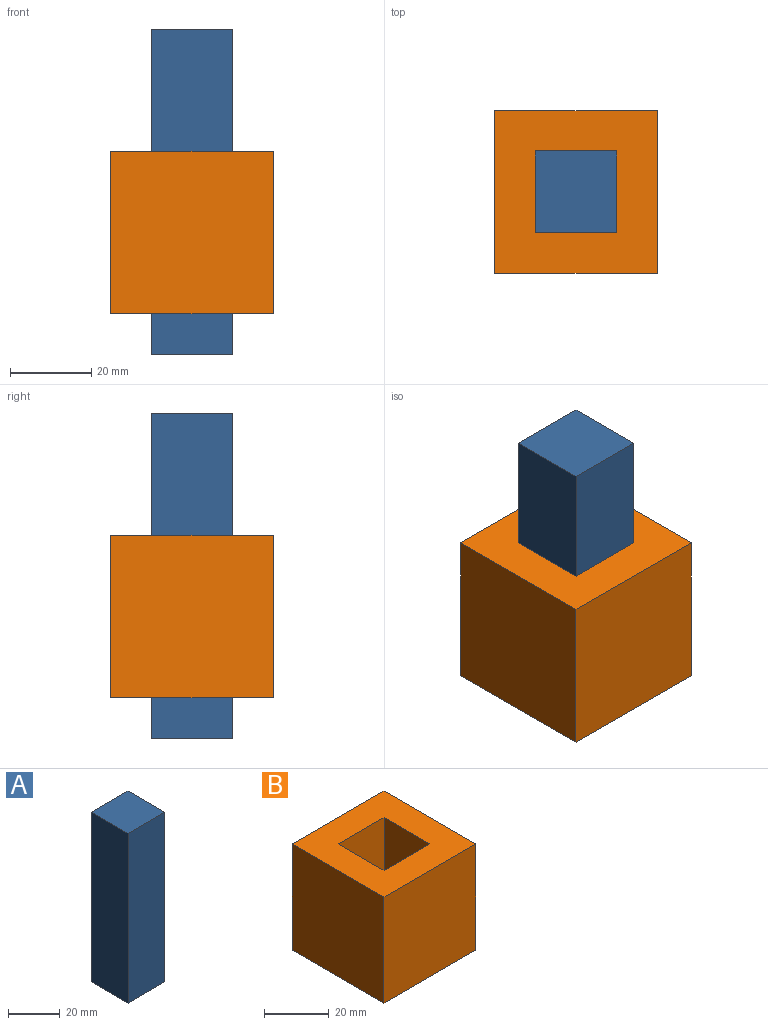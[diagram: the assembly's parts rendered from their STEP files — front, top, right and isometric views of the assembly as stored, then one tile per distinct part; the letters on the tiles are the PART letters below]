
ASSEMBLY  parts=2 mates=1
PART A: 6 faces, bbox 20x20x80 mm
  f0: plane 20x20mm, normal (0,0,-1), area 400mm2, adj f1,f3,f4,f5
  f1: plane 80x20mm, normal (1,0,0), area 1600mm2, adj f0,f2,f4,f5
  f2: plane 20x20mm, normal (0,0,1), area 400mm2, adj f1,f3,f4,f5
  f3: plane 80x20mm, normal (-1,0,0), area 1600mm2, adj f0,f2,f4,f5
  f4: plane 80x20mm, normal (0,-1,0), area 1600mm2, adj f0,f1,f2,f3
  f5: plane 80x20mm, normal (0,1,0), area 1600mm2, adj f0,f1,f2,f3
PART B: 10 faces, bbox 40x40x40 mm
  f0: plane 40x20mm, normal (-1,0,0), area 800mm2, adj f2,f3,f5,f9
  f1: plane 40x20mm, normal (1,0,0), area 800mm2, adj f2,f3,f5,f9
  f2: plane 40x20mm, normal (0,-1,0), area 800mm2, adj f0,f1,f3,f5
  f3: plane 40x40mm, normal (0,0,-1), area 1200mm2, adj f0,f1,f2,f4,f6,f7,f8,f9
  f4: plane 40x40mm, normal (-1,0,0), area 1600mm2, adj f3,f5,f7,f8
  f5: plane 40x40mm, normal (0,0,1), area 1200mm2, adj f0,f1,f2,f4,f6,f7,f8,f9
  f6: plane 40x40mm, normal (1,0,0), area 1600mm2, adj f3,f5,f7,f8
  f7: plane 40x40mm, normal (0,1,0), area 1600mm2, adj f3,f4,f5,f6
  f8: plane 40x40mm, normal (0,-1,0), area 1600mm2, adj f3,f4,f5,f6
  f9: plane 40x20mm, normal (0,1,0), area 800mm2, adj f0,f1,f3,f5
PLACE A t=(-27.54,-7.6,27.45)mm
PLACE B t=(-27.54,-7.6,17.45)mm fixed
MATE slider B.f5 <-> A.f2  axis (0,0,1) through (-27.54,-17.6,37.45)mm
